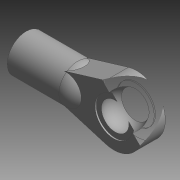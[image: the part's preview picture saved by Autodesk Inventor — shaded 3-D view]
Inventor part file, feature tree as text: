
AUTODESK INVENTOR PART (.ipt)
format: ipt  version: 2014 SP1 (Build 180222100, 222)  size: 132,608 bytes
history: native  units: in
note: dims shown in document units (in); Inventor stores cm internally (conversion verified against a paired STEP export)
features: sketch x6, extrude x5, revolve x1, fillet x1, boolean_combine x1
ambient origin geometry x8: Origin, YZ Plane, XZ Plane, XY Plane, X Axis, Y Axis, Z Axis, Center Point
bodies: Solid1 (feature_tree), Solid2 (feature_tree)
feature tree (14):
  sketch  "Sketch1"  dims[d0=0.4193in d2=0.2756in]
  extrude  "Extrusion1"  Depth=0.2756in
  extrude  "Extrusion2"  Depth=0.1673in
  revolve  "Revolution1"  [1 undecoded]
  extrude  "Extrusion3"  Depth=0.2756in
  extrude  "Extrusion4"  Depth=0.2096in TaperAngle=0.0deg
  fillet  "Fillet1"  Radius=0.1378in
  boolean_combine  "Combine1"
  extrude  "Extrusion5"  Depth=0.3937in TaperAngle=0.0deg
  sketch  "Sketch2"  dims[d3=0.1673in d4=0.0in d5=0.2756in]
  sketch  "Sketch3"  dims[d6=0.1476in d7=0.0in d8=0.25in]
  sketch  "Sketch4"  dims[d9=360.0deg d10=0.2756in]
  sketch  "Sketch5"  dims[d11=0.3937in d12=0.0in d13=0.2096in d14=0.0in d15=0.1378in]
  sketch  "Sketch6"  dims[d16=0.1299in d17=0.3937in d18=0.0in]
note: 1 required parameter value undecoded (feature->parameter linkage not recoverable at this tier; creation-order binding heuristic only, values carry confidence <= 0.55)
